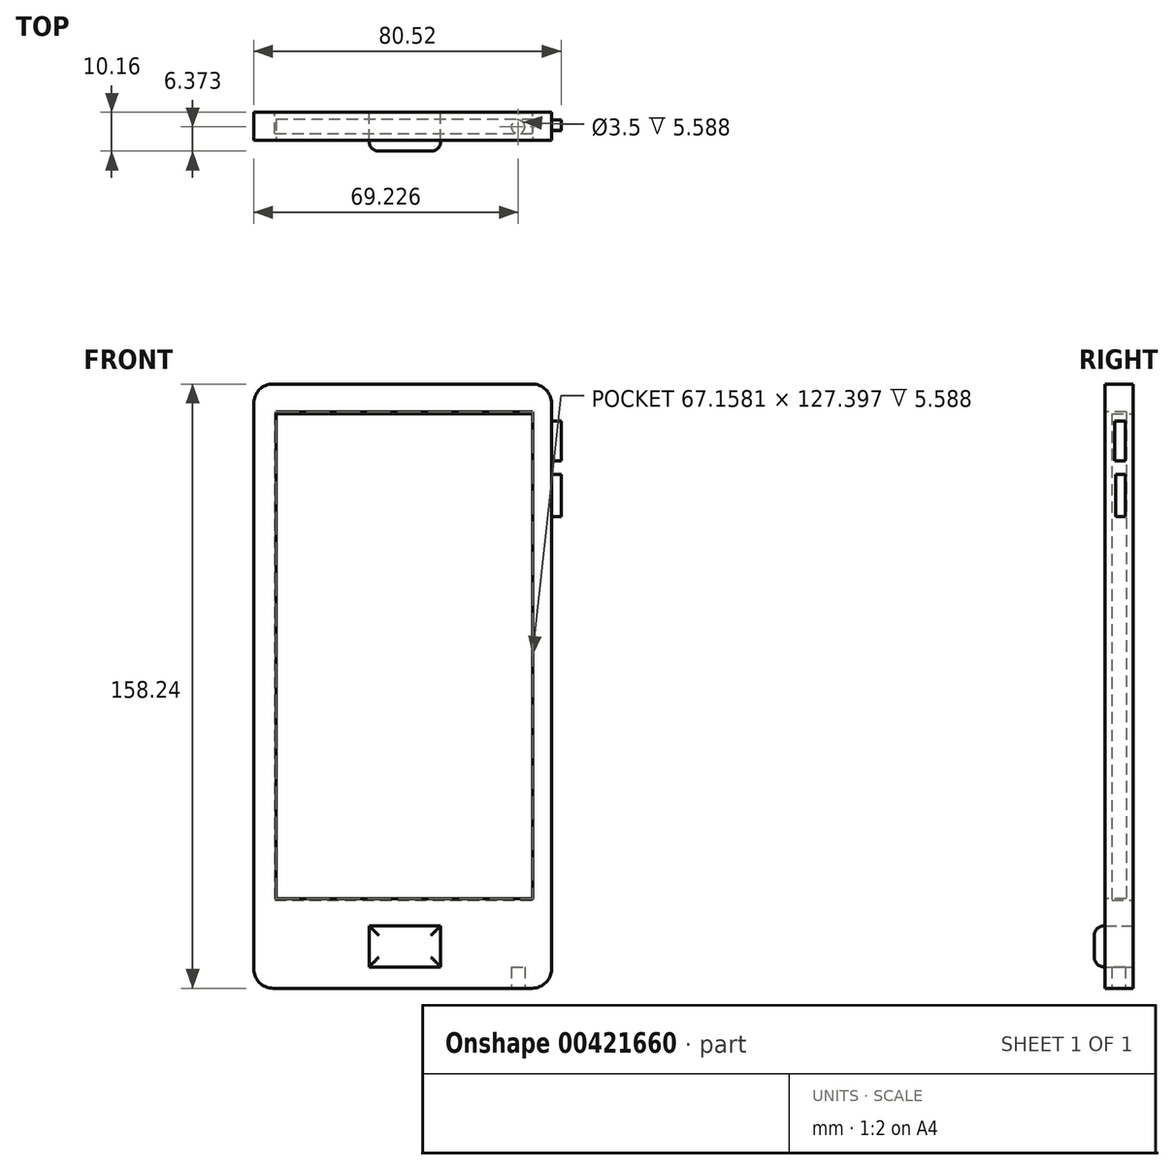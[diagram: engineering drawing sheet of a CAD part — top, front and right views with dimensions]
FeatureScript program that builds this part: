
annotation { "Feature Type Name" : "Feature", "Feature Type Description" : "" }
export const myFeature = defineFeature(function(context is Context, id is Id, definition is map)
    precondition{}
    {
        {
            var Q0;
            Q0=qCreatedBy(makeId("Front.planeOp"),FACE);
            var sketch = newSketch(context, id + "F0", { "sketchPlane" : qUnion([Q0])});
            skLineSegment(sketch, "E0.bottom", {"start": v(-34.24, 101.43) * mm, "end": v(43.74, 101.43) * mm});
            skLineSegment(sketch, "E0.top", {"start": v(-34.24, -56.8) * mm, "end": v(43.74, -56.8) * mm});
            skLineSegment(sketch, "E0.left", {"start": v(-34.24, 101.43) * mm, "end": v(-34.24, -56.8) * mm});
            skLineSegment(sketch, "E0.right", {"start": v(43.74, 101.43) * mm, "end": v(43.74, -56.8) * mm});
            skSolve(sketch);
        }
        {
            var Q0;
            Q0 = qSketchRegion(id + "F0", true);
            extrude(context, id + "F1", {"entities" : qUnion([Q0]), "depth" : 7.37 * mm});
        }
        {
            var Q0;
            Q0=makeQuery(id+"F1.opExtrude","CAP_FACE",FACE,{"disambiguationData":[OSD([sQuery(id+"F0.wireOp",EDGE,"E0.bottom"),sQuery(id+"F0.wireOp",EDGE,"E0.top"),sQuery(id+"F0.wireOp",EDGE,"E0.left"),sQuery(id+"F0.wireOp",EDGE,"E0.right")])],"isStart":false});
            var sketch = newSketch(context, id + "F2", { "sketchPlane" : qUnion([Q0])});
            skLineSegment(sketch, "E1.bottom", {"start": v(-28.35, 94.08) * mm, "end": v(38.8, 94.08) * mm});
            skLineSegment(sketch, "E1.top", {"start": v(-28.35, -33.31) * mm, "end": v(38.8, -33.31) * mm});
            skLineSegment(sketch, "E1.left", {"start": v(-28.35, 94.08) * mm, "end": v(-28.35, -33.31) * mm});
            skLineSegment(sketch, "E1.right", {"start": v(38.8, 94.08) * mm, "end": v(38.8, -33.31) * mm});
            skSolve(sketch);
        }
        {
            var Q0;
            Q0 = qSketchRegion(id + "F2", true);
            extrude(context, id + "F3", {"entities" : qUnion([Q0]), "operationType" : NewBodyOperationType.REMOVE, "oppositeDirection" : true, "depth" : 5.6 * mm});
        }
        {
            var Q0;
            Q0=qCreatedBy(makeId("Front.planeOp"),FACE);
            var sketch = newSketch(context, id + "F4", { "sketchPlane" : qUnion([Q0])});
            skLineSegment(sketch, "E2.bottom", {"start": v(-28.76, 93.68) * mm, "end": v(38.8, 93.68) * mm});
            skLineSegment(sketch, "E2.top", {"start": v(-28.76, -33.72) * mm, "end": v(38.8, -33.72) * mm});
            skLineSegment(sketch, "E2.left", {"start": v(-28.76, 93.68) * mm, "end": v(-28.76, -33.72) * mm});
            skLineSegment(sketch, "E2.right", {"start": v(38.8, 93.68) * mm, "end": v(38.8, -33.72) * mm});
            skSolve(sketch);
        }
        {
            var Q0;
            Q0 = qSketchRegion(id + "F4", true);
            extrude(context, id + "F5", {"entities" : qUnion([Q0]), "depth" : 5.6 * mm});
        }
        {
            var Q0;
            Q0=makeQuery(id+"F1.opExtrude","SWEPT_EDGE",EDGE,{"disambiguationData":[OSD([sQuery(id+"F0.wireOp",EDGE,"E0.bottom"),sQuery(id+"F0.wireOp",EDGE,"E0.left")])]});
            fillet(context, id + "F6", {"entities" : qUnion([Q0]), "radius" : 5.08 * mm, "tangentPropagation" : true, "allowEdgeOverflow" : false});
        }
        {
            var Q0;
            Q0=makeQuery(id+"F1.opExtrude","SWEPT_EDGE",EDGE,{"disambiguationData":[OSD([sQuery(id+"F0.wireOp",EDGE,"E0.bottom"),sQuery(id+"F0.wireOp",EDGE,"E0.right")])]});
            fillet(context, id + "F7", {"entities" : qUnion([Q0]), "radius" : 5.08 * mm, "tangentPropagation" : true, "allowEdgeOverflow" : false});
        }
        {
            var Q0;
            Q0=makeQuery(id+"F1.opExtrude","SWEPT_EDGE",EDGE,{"disambiguationData":[OSD([sQuery(id+"F0.wireOp",EDGE,"E0.top"),sQuery(id+"F0.wireOp",EDGE,"E0.right")])]});
            fillet(context, id + "F8", {"entities" : qUnion([Q0]), "radius" : 5.08 * mm, "tangentPropagation" : true, "allowEdgeOverflow" : false});
        }
        {
            var Q0;
            Q0=makeQuery(id+"F1.opExtrude","SWEPT_EDGE",EDGE,{"disambiguationData":[OSD([sQuery(id+"F0.wireOp",EDGE,"E0.top"),sQuery(id+"F0.wireOp",EDGE,"E0.left")])]});
            fillet(context, id + "F9", {"entities" : qUnion([Q0]), "radius" : 5.08 * mm, "tangentPropagation" : true, "allowEdgeOverflow" : false});
        }
        {
            var Q0;
            Q0=makeQuery(id+"F1.opExtrude","SWEPT_FACE",FACE,{"disambiguationData":[OSD([sQuery(id+"F0.wireOp",EDGE,"E0.top")])]});
            var sketch = newSketch(context, id + "F10", { "sketchPlane" : qUnion([Q0])});
            skCircle(sketch, "E3", {"center": v(34.99, 3.79) * mm, "radius": 1.75 * mm});
            skSolve(sketch);
        }
        {
            var Q0;
            Q0 = qSketchRegion(id + "F10", true);
            extrude(context, id + "F11", {"entities" : qUnion([Q0]), "operationType" : NewBodyOperationType.REMOVE, "oppositeDirection" : true, "depth" : 5.6 * mm});
        }
        {
            var Q0;
            Q0=makeQuery(id+"F1.opExtrude","SWEPT_FACE",FACE,{"disambiguationData":[OSD([sQuery(id+"F0.wireOp",EDGE,"E0.right")])]});
            var sketch = newSketch(context, id + "F12", { "sketchPlane" : qUnion([Q0])});
            skLineSegment(sketch, "E4.bottom", {"start": v(-4.83, 91.76) * mm, "end": v(-1.99, 91.76) * mm});
            skLineSegment(sketch, "E4.top", {"start": v(-4.83, 81.28) * mm, "end": v(-1.99, 81.28) * mm});
            skLineSegment(sketch, "E4.left", {"start": v(-4.83, 91.76) * mm, "end": v(-4.83, 81.28) * mm});
            skLineSegment(sketch, "E4.right", {"start": v(-1.99, 91.76) * mm, "end": v(-1.99, 81.28) * mm});
            skLineSegment(sketch, "E5.bottom", {"start": v(-4.54, 77.76) * mm, "end": v(-1.99, 77.76) * mm});
            skLineSegment(sketch, "E5.top", {"start": v(-4.54, 66.65) * mm, "end": v(-1.99, 66.65) * mm});
            skLineSegment(sketch, "E5.left", {"start": v(-4.54, 77.76) * mm, "end": v(-4.54, 66.65) * mm});
            skLineSegment(sketch, "E5.right", {"start": v(-1.99, 77.76) * mm, "end": v(-1.99, 66.65) * mm});
            skSolve(sketch);
        }
        {
            var Q0;
            Q0 = qSketchRegion(id + "F12", true);
            extrude(context, id + "F13", {"entities" : qUnion([Q0]), "depth" : 2.54 * mm});
        }
        {
            var Q0;
            Q0=qCreatedBy(makeId("Front.planeOp"),FACE);
            var sketch = newSketch(context, id + "F14", { "sketchPlane" : qUnion([Q0])});
            skLineSegment(sketch, "E6.bottom", {"start": v(-4.01, -40.45) * mm, "end": v(14.74, -40.45) * mm});
            skLineSegment(sketch, "E6.top", {"start": v(-4.01, -51.22) * mm, "end": v(14.74, -51.22) * mm});
            skLineSegment(sketch, "E6.left", {"start": v(-4.01, -40.45) * mm, "end": v(-4.01, -51.22) * mm});
            skLineSegment(sketch, "E6.right", {"start": v(14.74, -40.45) * mm, "end": v(14.74, -51.22) * mm});
            skSolve(sketch);
        }
        {
            var Q0;
            Q0 = qSketchRegion(id + "F14", true);
            extrude(context, id + "F15", {"entities" : qUnion([Q0]), "depth" : 10.16 * mm});
        }
        {
            var Q0;
            Q0=makeQuery(id+"F15.opExtrude","CAP_EDGE",EDGE,{"disambiguationData":[OSD([sQuery(id+"F14.wireOp",EDGE,"E6.bottom")])],"isStart":false});
            var Q1;
            Q1=makeQuery(id+"F15.opExtrude","CAP_EDGE",EDGE,{"disambiguationData":[OSD([sQuery(id+"F14.wireOp",EDGE,"E6.left")])],"isStart":false});
            var Q2;
            Q2=makeQuery(id+"F15.opExtrude","CAP_EDGE",EDGE,{"disambiguationData":[OSD([sQuery(id+"F14.wireOp",EDGE,"E6.right")])],"isStart":false});
            var Q3;
            Q3=makeQuery(id+"F15.opExtrude","CAP_EDGE",EDGE,{"disambiguationData":[OSD([sQuery(id+"F14.wireOp",EDGE,"E6.top")])],"isStart":false});
            fillet(context, id + "F16", {"entities" : qUnion([Q0, Q1, Q2, Q3]), "radius" : 2.54 * mm, "tangentPropagation" : true, "allowEdgeOverflow" : false});
        }
    });
